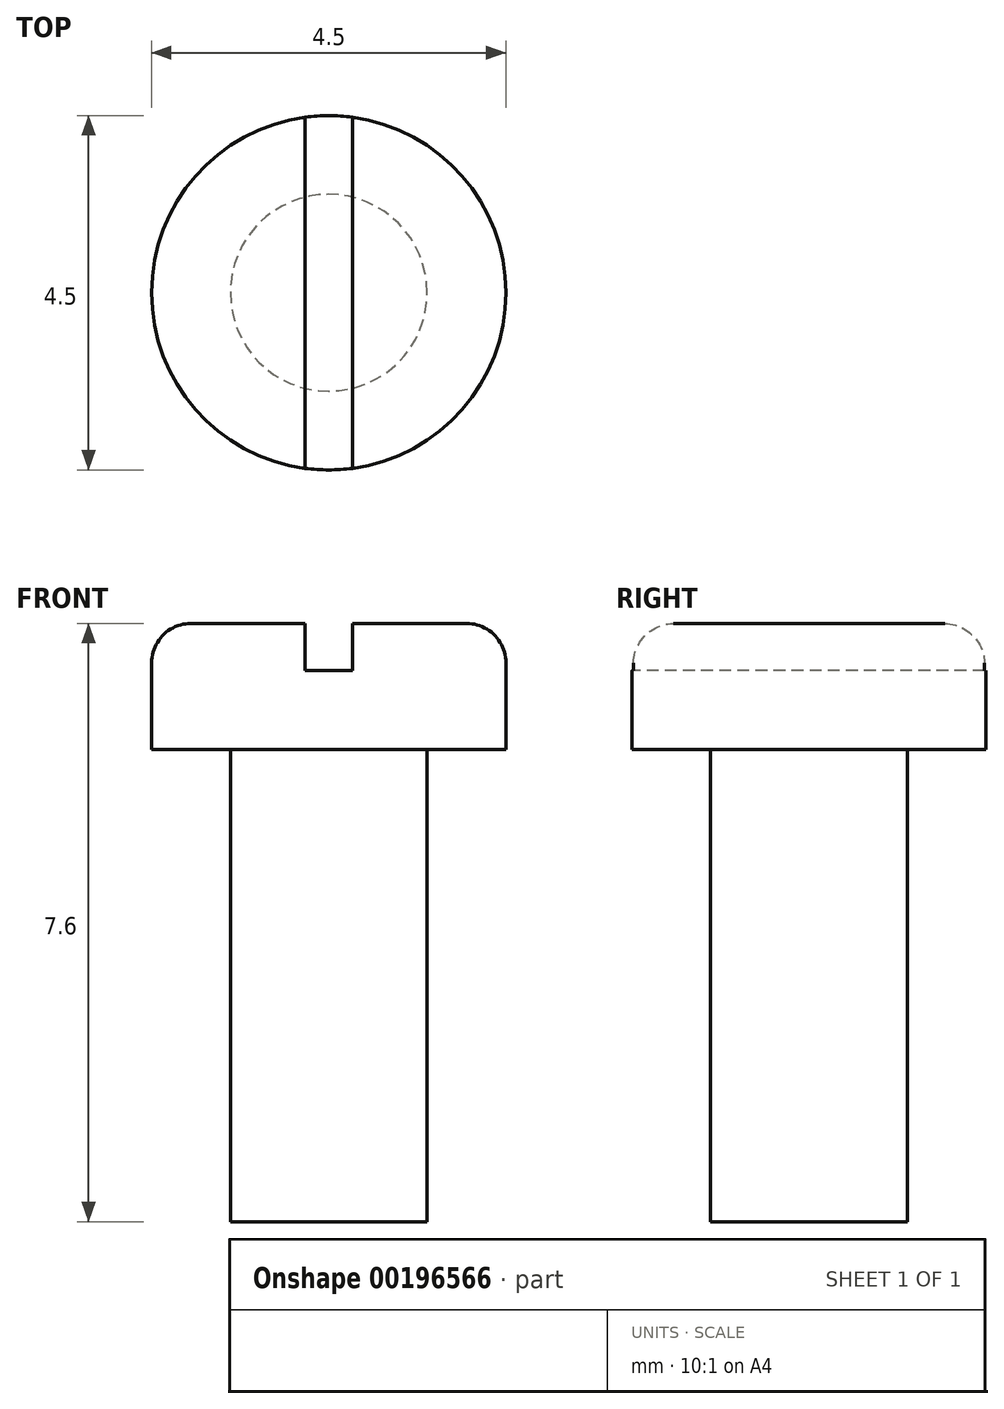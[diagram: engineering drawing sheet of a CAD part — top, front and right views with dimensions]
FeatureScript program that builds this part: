
annotation { "Feature Type Name" : "Feature", "Feature Type Description" : "" }
export const myFeature = defineFeature(function(context is Context, id is Id, definition is map)
    precondition{}
    {
        {
            var Q0;
            Q0=qCreatedBy(makeId("Front.planeOp"),FACE);
            var sketch = newSketch(context, id + "F0", { "sketchPlane" : qUnion([Q0])});
            skLineSegment(sketch, "E0", {"start": v(0, 1.6) * mm, "end": v(1.75, 1.6) * mm});
            skLineSegment(sketch, "E1", {"start": v(2.25, 1.1) * mm, "end": v(2.25, 0) * mm});
            skLineSegment(sketch, "E2", {"start": v(2.25, 0) * mm, "end": v(1.25, 0) * mm});
            skLineSegment(sketch, "E3", {"start": v(1.25, 0) * mm, "end": v(1.25, -6) * mm});
            skLineSegment(sketch, "E4", {"start": v(1.25, -6) * mm, "end": v(0, -6) * mm});
            skLineSegment(sketch, "E5", {"start": v(0, -6) * mm, "end": v(0, 1.6) * mm});
            skLineSegment(sketch, "E6", {"start": v(0, 0) * mm, "end": v(0, 3.3) * mm, "construction": true});
            skPoint(sketch, "E7.visualSharp", {"position": v(2.25, 1.6) * mm});
            skArc(sketch, "E7.filletArc", {"start": v(2.25, 1.1) * mm, "mid": v(2.1, 1.45) * mm, "end": v(1.75, 1.6) * mm});
            skSolve(sketch);
        }
        {
            var Q0;
            Q0=qSketchRegion(id+"F0",true);
            var Q1;
            Q1=sQuery(id+"F0.wireOp",EDGE,"E6");
            revolve(context, id + "F1", {"entities" : qUnion([Q0]), "axis" : qUnion([Q1]), "revolveType" : RevolveType.FULL});
        }
        {
            var Q0;
            Q0=qCreatedBy(makeId("Front.planeOp"),FACE);
            var sketch = newSketch(context, id + "F2", { "sketchPlane" : qUnion([Q0])});
            skLineSegment(sketch, "E8.bottom", {"start": v(0.3, 1) * mm, "end": v(-0.3, 1) * mm});
            skLineSegment(sketch, "E8.top", {"start": v(0.3, 1.6) * mm, "end": v(-0.3, 1.6) * mm});
            skLineSegment(sketch, "E8.left", {"start": v(0.3, 1) * mm, "end": v(0.3, 1.6) * mm});
            skLineSegment(sketch, "E8.right", {"start": v(-0.3, 1) * mm, "end": v(-0.3, 1.6) * mm});
            skPoint(sketch, "E8.middle", {"position": v(0, 1.3) * mm});
            skSolve(sketch);
        }
        {
            var Q0;
            Q0=qSketchRegion(id+"F2",true);
            extrude(context, id + "F3", {"entities" : qUnion([Q0]), "operationType" : NewBodyOperationType.REMOVE, "endBound" : BoundingType.THROUGH_ALL, "oppositeDirection" : true, "depth" : 25 * mm, "hasSecondDirection" : true, "secondDirectionBound" : SecondDirectionBoundingType.THROUGH_ALL, "secondDirectionOppositeDirection" : false, "secondDirectionDepth" : 25 * mm});
        }
    });
